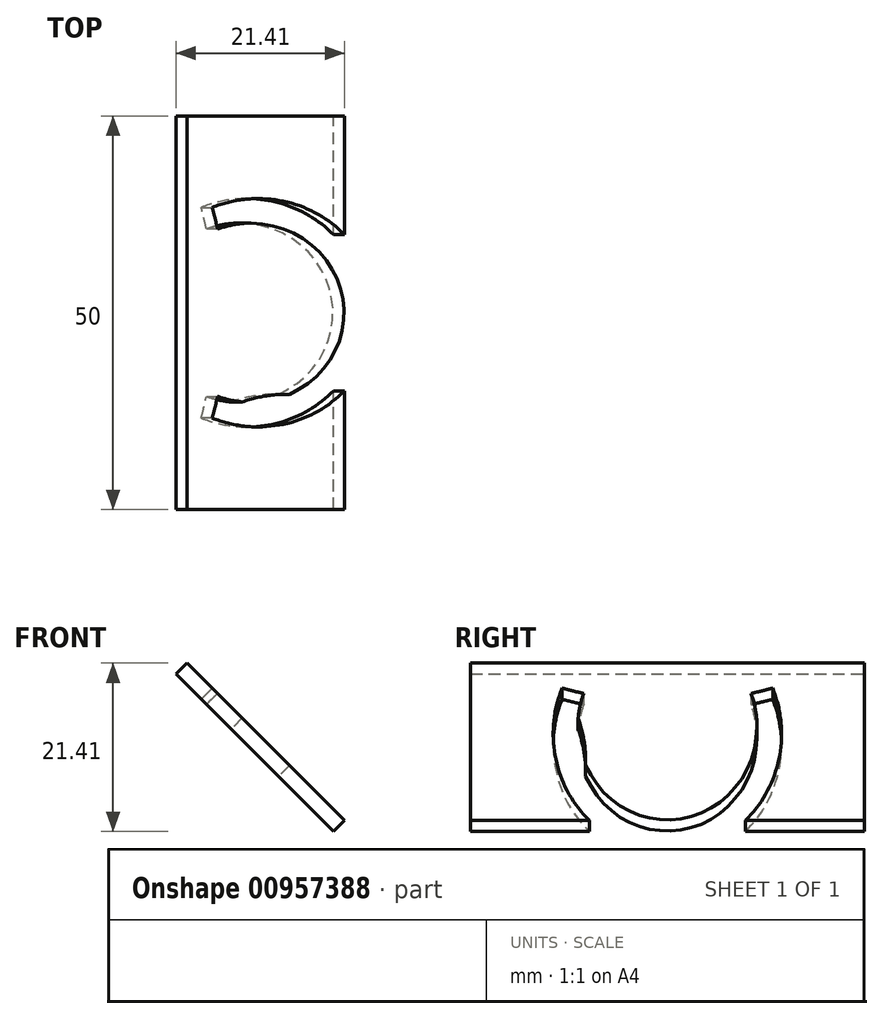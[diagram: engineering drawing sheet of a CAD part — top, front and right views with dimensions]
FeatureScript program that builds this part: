
annotation { "Feature Type Name" : "Feature", "Feature Type Description" : "" }
export const myFeature = defineFeature(function(context is Context, id is Id, definition is map)
    precondition{}
    {
        {
            var Q0;
            Q0=qCreatedBy(makeId("Front.planeOp"),FACE);
            var sketch = newSketch(context, id + "F0", { "sketchPlane" : qUnion([Q0])});
            skLineSegment(sketch, "E0", {"start": v(-15, 0) * mm, "end": v(-18, 0) * mm});
            skLineSegment(sketch, "E1", {"start": v(-18, 0) * mm, "end": v(0, 67.18) * mm});
            skLineSegment(sketch, "E2", {"start": v(0, 67.18) * mm, "end": v(0, 55.98) * mm});
            skLineSegment(sketch, "E3", {"start": v(0, 55.98) * mm, "end": v(-15, 0) * mm});
            skLineSegment(sketch, "E4", {"start": v(0, 0) * mm, "end": v(0, -11.34) * mm});
            skSolve(sketch);
        }
        {
            var Q0;
            Q0=qSketchRegion(id+"F0",true);
            var Q1;
            Q1=sQuery(id+"F0.wireOp",EDGE,"E4");
            revolve(context, id + "F1", {"surfaceOperationType" : NewSurfaceOperationType.NEW, "entities" : qUnion([Q0]), "axis" : qUnion([Q1]), "revolveType" : RevolveType.FULL});
        }
        {
            var Q0;
            Q0=qCreatedBy(makeId("Front.planeOp"),FACE);
            var sketch = newSketch(context, id + "F2", { "sketchPlane" : qUnion([Q0])});
            skLineSegment(sketch, "E5", {"start": v(0, 0) * mm, "end": v(-51.1, 0) * mm});
            skLineSegment(sketch, "E6", {"start": v(-51.1, 0) * mm, "end": v(-51.1, 70) * mm});
            skLineSegment(sketch, "E7", {"start": v(-51.1, 70) * mm, "end": v(0, 70) * mm});
            skLineSegment(sketch, "E8", {"start": v(0, 70) * mm, "end": v(0, 0) * mm});
            skSolve(sketch);
        }
        {
            var Q0;
            Q0=makeQuery(id+"F2.imprint","IMPRINT",FACE,{"disambiguationData":[TD([[makeQuery(id+"F2.imprint","IMPRINT",EDGE,{"derivedFrom":sQuery(id+"F2.wireOp",EDGE,"E5")}),-1.0]])]});
            var Q1;
            Q1=sQuery(id+"F2.wireOp",EDGE,"E6");
            revolve(context, id + "F3", {"operationType" : NewBodyOperationType.REMOVE, "surfaceOperationType" : NewSurfaceOperationType.NEW, "entities" : qUnion([Q0]), "axis" : qUnion([Q1]), "revolveType" : RevolveType.FULL, "oppositeDirection" : true});
        }
        {
            var Q0;
            Q0=qCreatedBy(makeId("Front.planeOp"),FACE);
            var sketch = newSketch(context, id + "F4", { "sketchPlane" : qUnion([Q0])});
            skLineSegment(sketch, "E9", {"start": v(13.6, 0) * mm, "end": v(-5.68, 19.29) * mm});
            skLineSegment(sketch, "E10", {"start": v(-5.68, 19.29) * mm, "end": v(-4.97, 20) * mm});
            skLineSegment(sketch, "E11", {"start": v(-4.97, 20) * mm, "end": v(15.02, 0) * mm});
            skLineSegment(sketch, "E12", {"start": v(13.6, 0) * mm, "end": v(15.02, 0) * mm});
            skSolve(sketch);
        }
        {
            var Q0;
            Q0 = qSketchRegion(id + "F4", true);
            extrude(context, id + "F5", {"entities" : qUnion([Q0]), "endBound" : BoundingType.SYMMETRIC, "depth" : 50 * mm, "offsetDistance" : 25 * mm});
        }
        {
            var Q0;
            Q0=makeQuery(id+"F1.opRevolve","SWEPT_BODY",BODY,{"disambiguationData":[OSD([sQuery(id+"F0.wireOp",EDGE,"E0"),sQuery(id+"F0.wireOp",EDGE,"E1"),sQuery(id+"F0.wireOp",EDGE,"E2"),sQuery(id+"F0.wireOp",EDGE,"E3")])]});
            var Q1;
            Q1=makeQuery(id+"F5.opExtrude","SWEPT_BODY",BODY,{"disambiguationData":[OSD([sQuery(id+"F4.wireOp",EDGE,"E9"),sQuery(id+"F4.wireOp",EDGE,"E10"),sQuery(id+"F4.wireOp",EDGE,"E11"),sQuery(id+"F4.wireOp",EDGE,"E12")])]});
            booleanBodies(context, id + "F6", {"operationType" : BooleanOperationType.SUBTRACTION, "tools" : qUnion([Q0]), "targets" : qUnion([Q1])});
        }
        {
            var Q0;
            Q0=makeQuery(id+"F5.opExtrude","SWEPT_FACE",FACE,{"disambiguationData":[OSD([sQuery(id+"F4.wireOp",EDGE,"E11")])]});
            var sketch = newSketch(context, id + "F7", { "sketchPlane" : qUnion([Q0])});
            skArc(sketch, "E13", {"start": v(-12.2, -10.62) * mm, "mid": v(-10.37, 0) * mm, "end": v(-12.2, 10.62) * mm});
            skSolve(sketch);
        }
        {
            var Q0;
            Q0=makeQuery(id+"F7.imprint","IMPRINT",FACE,{"disambiguationData":[TD([[makeQuery(id+"F7.imprint","IMPRINT",EDGE,{"derivedFrom":sQuery(id+"F7.wireOp",EDGE,"E13")}),-1.0]])]});
            extrude(context, id + "F8", {"entities" : qUnion([Q0]), "depth" : 2 * mm, "offsetDistance" : 25 * mm});
        }
        {
            var Q0;
            Q0=makeQuery(id+"F5.opExtrude","SWEPT_BODY",BODY,{"disambiguationData":[OSD([sQuery(id+"F4.wireOp",EDGE,"E9"),sQuery(id+"F4.wireOp",EDGE,"E10"),sQuery(id+"F4.wireOp",EDGE,"E11"),sQuery(id+"F4.wireOp",EDGE,"E12")])]});
            deleteBodies(context, id + "F9", {"entities" : qUnion([Q0])});
        }
    });
